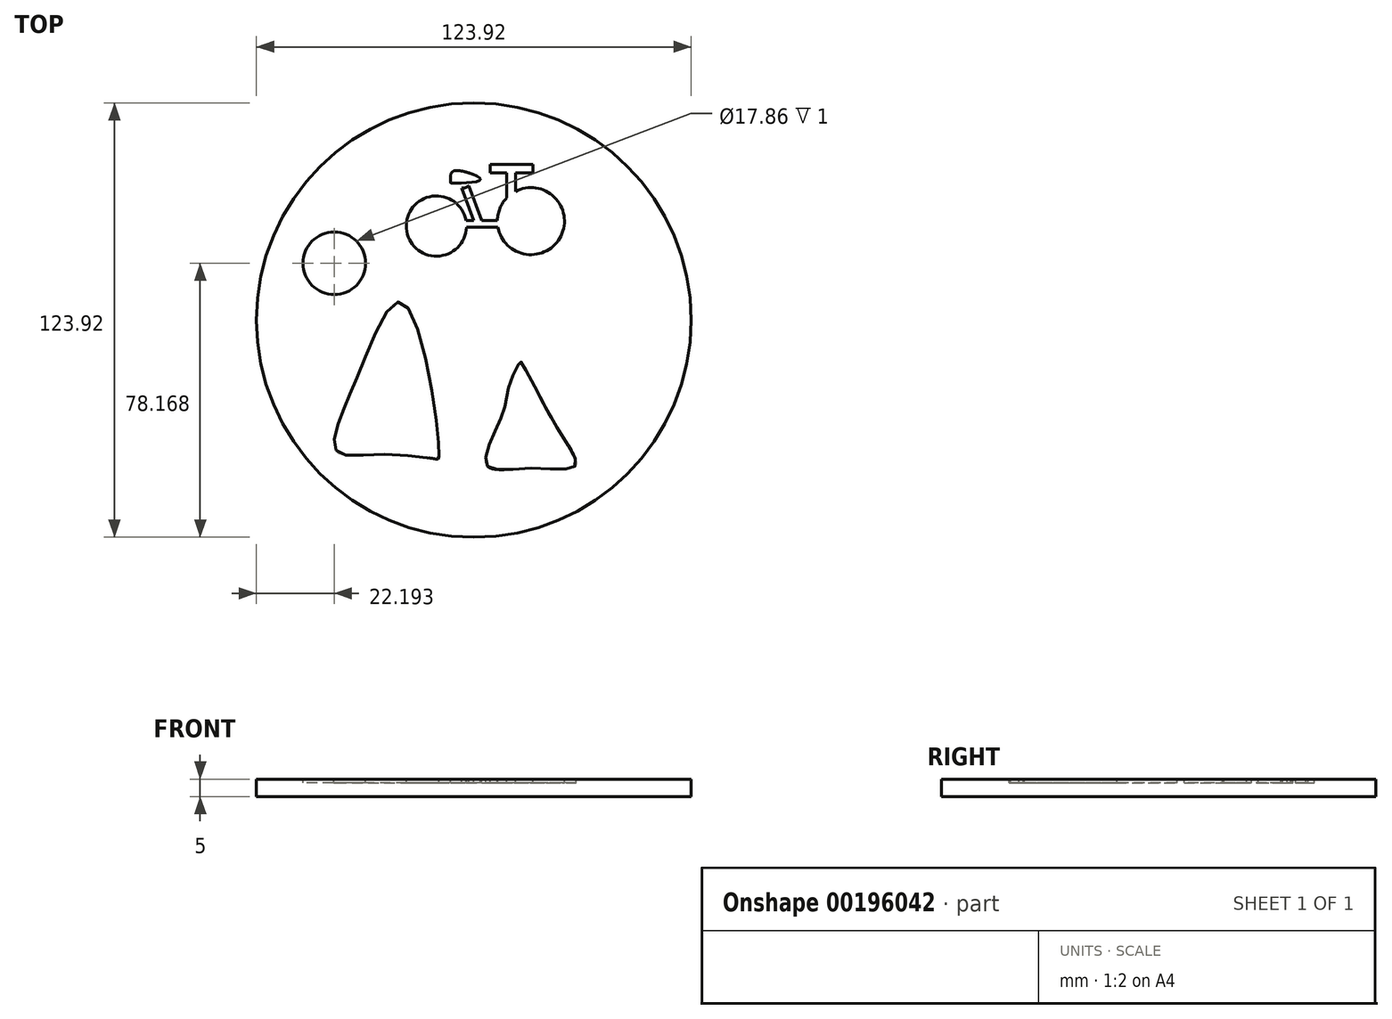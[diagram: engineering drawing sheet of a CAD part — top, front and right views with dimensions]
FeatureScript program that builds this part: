
annotation { "Feature Type Name" : "Feature", "Feature Type Description" : "" }
export const myFeature = defineFeature(function(context is Context, id is Id, definition is map)
    precondition{}
    {
        {
            var Q0;
            Q0=qCreatedBy(makeId("Top.planeOp"),FACE);
            var sketch = newSketch(context, id + "F0", { "sketchPlane" : qUnion([Q0])});
            skCircle(sketch, "E0", {"center": v(0, 0) * mm, "radius": 61.96 * mm});
            skSolve(sketch);
        }
        {
            var Q0;
            Q0 = qSketchRegion(id + "F0", true);
            extrude(context, id + "F1", {"entities" : qUnion([Q0]), "depth" : 5 * mm});
        }
        {
            var Q0;
            Q0=makeQuery(id+"F1.opExtrude","CAP_FACE",FACE,{"disambiguationData":[OSD([sQuery(id+"F0.wireOp",EDGE,"E0")])],"isStart":false});
            var sketch = newSketch(context, id + "F2", { "sketchPlane" : qUnion([Q0])});
            skFitSpline(sketch, "E1", {"points": [v(-39.3, -37.2) * mm, v(-26.67, -38.32) * mm, v(-10.39, -39.73) * mm, v(-10.1, -39.73) * mm, v(-10.95, -26.53) * mm, v(-21.06, 5.2) * mm, v(-32, -13.34) * mm, v(-37.9, -27.37) * mm, v(-39.3, -37.2) * mm]});
            skFitSpline(sketch, "E2", {"points": [v(3.93, -41.7) * mm, v(5.05, -34.11) * mm, v(8.98, -24.28) * mm, v(10.1, -18.67) * mm, v(13.2, -11.93) * mm, v(13.48, -11.93) * mm, v(23.3, -29.9) * mm, v(28.92, -41.7) * mm, v(16.84, -42.25) * mm, v(3.93, -41.7) * mm]});
            skSolve(sketch);
        }
        {
            var Q0;
            Q0=makeQuery(id+"F2.imprint","IMPRINT",FACE,{"disambiguationData":[TD([[makeQuery(id+"F2.imprint","IMPRINT",EDGE,{"derivedFrom":sQuery(id+"F2.wireOp",EDGE,"E1")}),1.0]])]});
            var Q1;
            Q1=makeQuery(id+"F2.imprint","IMPRINT",FACE,{"disambiguationData":[TD([[makeQuery(id+"F2.imprint","IMPRINT",EDGE,{"derivedFrom":sQuery(id+"F2.wireOp",EDGE,"E2")}),-1.0]])]});
            extrude(context, id + "F3", {"entities" : qUnion([Q0, Q1]), "operationType" : NewBodyOperationType.REMOVE, "oppositeDirection" : true, "depth" : 1 * mm});
        }
        {
            var Q0;
            Q0=makeQuery(id+"F1.opExtrude","CAP_FACE",FACE,{"disambiguationData":[OSD([sQuery(id+"F0.wireOp",EDGE,"E0")])],"isStart":false});
            var sketch = newSketch(context, id + "F4", { "sketchPlane" : qUnion([Q0])});
            skCircle(sketch, "E3", {"center": v(-10.67, 26.81) * mm, "radius": 8.6 * mm});
            skCircle(sketch, "E4", {"center": v(16.28, 28.21) * mm, "radius": 9.56 * mm});
            skLineSegment(sketch, "E5", {"start": v(-2.08, 26.52) * mm, "end": v(6.87, 26.52) * mm});
            skLineSegment(sketch, "E6", {"start": v(-2.23, 28.45) * mm, "end": v(6.72, 28.45) * mm});
            skLineSegment(sketch, "E7", {"start": v(0, 28.45) * mm, "end": v(-3.44, 37.62) * mm});
            skPoint(sketch, "E7.startSnap0", {"position": v(2.25, 28.45) * mm});
            skLineSegment(sketch, "E8", {"start": v(2.25, 28.45) * mm, "end": v(-1.47, 38.32) * mm});
            skLineSegment(sketch, "E9", {"start": v(-1.47, 38.32) * mm, "end": v(-3.44, 37.62) * mm});
            skFitSpline(sketch, "E10", {"points": [v(-3.44, 37.62) * mm, v(-7.8, 37.62) * mm, v(1.9, 42.95) * mm, v(-1.47, 38.32) * mm, v(-3.44, 37.62) * mm]});
            skLineSegment(sketch, "E11", {"start": v(9.4, 34.86) * mm, "end": v(9.4, 41.97) * mm});
            skLineSegment(sketch, "E12", {"start": v(9.4, 41.97) * mm, "end": v(11.86, 41.97) * mm});
            skLineSegment(sketch, "E13", {"start": v(11.86, 41.97) * mm, "end": v(11.86, 36.7) * mm});
            skLineSegment(sketch, "E14", {"start": v(11.86, 41.97) * mm, "end": v(16.92, 41.97) * mm});
            skLineSegment(sketch, "E15", {"start": v(16.92, 41.97) * mm, "end": v(16.92, 44.36) * mm});
            skLineSegment(sketch, "E16", {"start": v(16.92, 44.36) * mm, "end": v(4.7, 44.36) * mm});
            skLineSegment(sketch, "E17", {"start": v(4.7, 44.36) * mm, "end": v(4.7, 41.97) * mm});
            skLineSegment(sketch, "E18", {"start": v(4.7, 41.97) * mm, "end": v(9.4, 41.97) * mm});
            skCircle(sketch, "E19", {"center": v(-37.99, 16.8) * mm, "radius": 8.46 * mm});
            skLineSegment(sketch, "E20", {"start": v(-33.11, 26.42) * mm, "end": v(-28.01, 29.53) * mm});
            skLineSegment(sketch, "E21", {"start": v(-28.01, 29.53) * mm, "end": v(-30.73, 25.1) * mm});
            skLineSegment(sketch, "E22", {"start": v(-30.73, 25.1) * mm, "end": v(-33.11, 26.42) * mm});
            skLineSegment(sketch, "E23", {"start": v(-27.75, 19.93) * mm, "end": v(-27.75, 17.34) * mm});
            skLineSegment(sketch, "E24", {"start": v(-27.75, 17.34) * mm, "end": v(-22.05, 18.14) * mm});
            skLineSegment(sketch, "E25", {"start": v(-22.05, 18.14) * mm, "end": v(-27.75, 19.93) * mm});
            skLineSegment(sketch, "E26", {"start": v(-27.75, 12.24) * mm, "end": v(-29.07, 10) * mm});
            skLineSegment(sketch, "E27", {"start": v(-29.07, 10) * mm, "end": v(-22.78, 8.67) * mm});
            skLineSegment(sketch, "E28", {"start": v(-22.78, 8.67) * mm, "end": v(-27.75, 12.24) * mm});
            skLineSegment(sketch, "E29", {"start": v(-35.12, 5.65) * mm, "end": v(-30.16, 1.28) * mm});
            skLineSegment(sketch, "E30", {"start": v(-30.16, 1.28) * mm, "end": v(-32.28, 6.71) * mm});
            skLineSegment(sketch, "E31", {"start": v(-32.28, 6.71) * mm, "end": v(-35.12, 5.65) * mm});
            skLineSegment(sketch, "E32", {"start": v(-42.79, 7.18) * mm, "end": v(-40.55, 5.65) * mm});
            skLineSegment(sketch, "E33", {"start": v(-40.55, 5.65) * mm, "end": v(-43.67, 1.08) * mm});
            skLineSegment(sketch, "E34", {"start": v(-43.67, 1.08) * mm, "end": v(-42.79, 7.18) * mm});
            skSolve(sketch);
        }
        {
            var Q0;
            {var subQ0=sQuery(id+"F4.wireOp",EDGE,"E3");var subQ1=makeQuery(id+"F4.imprint","INTERSECT",VERTEX,{"derivedFrom":[subQ0,sQuery(id+"F4.wireOp",EDGE,"E5")]});Q0=makeQuery(id+"F4.imprint","IMPRINT",FACE,{"disambiguationData":[TD([[makeQuery(id+"F4.imprint","IMPRINT",EDGE,{"disambiguationData":[TD([[subQ1,1.0]])],"derivedFrom":subQ0}),1.0]])]});}
            var Q1;
            {var subQ0=sQuery(id+"F4.wireOp",EDGE,"E7");Q1=makeQuery(id+"F4.imprint","IMPRINT",FACE,{"disambiguationData":[TD([[makeQuery(id+"F4.imprint","IMPRINT",EDGE,{"derivedFrom":subQ0}),-1.0]])]});}
            var Q2;
            {var subQ0=sQuery(id+"F4.wireOp",EDGE,"E5");Q2=makeQuery(id+"F4.imprint","IMPRINT",FACE,{"disambiguationData":[TD([[makeQuery(id+"F4.imprint","IMPRINT",EDGE,{"derivedFrom":subQ0}),1.0]])]});}
            var Q3;
            {var subQ0=sQuery(id+"F4.wireOp",EDGE,"E4");var subQ1=makeQuery(id+"F4.imprint","INTERSECT",VERTEX,{"derivedFrom":[subQ0,sQuery(id+"F4.wireOp",EDGE,"E11")]});Q3=makeQuery(id+"F4.imprint","IMPRINT",FACE,{"disambiguationData":[TD([[makeQuery(id+"F4.imprint","IMPRINT",EDGE,{"disambiguationData":[TD([[subQ1,1.0]])],"derivedFrom":subQ0}),1.0]])]});}
            var Q4;
            {var subQ0=sQuery(id+"F4.wireOp",EDGE,"E11");Q4=makeQuery(id+"F4.imprint","IMPRINT",FACE,{"disambiguationData":[TD([[makeQuery(id+"F4.imprint","IMPRINT",EDGE,{"derivedFrom":subQ0}),-1.0]])]});}
            var Q5;
            Q5=makeQuery(id+"F4.imprint","IMPRINT",FACE,{"disambiguationData":[TD([[makeQuery(id+"F4.imprint","IMPRINT",EDGE,{"derivedFrom":sQuery(id+"F4.wireOp",EDGE,"E12")}),1.0]])]});
            extrude(context, id + "F5", {"entities" : qUnion([Q0, Q1, Q2, Q3, Q4, Q5]), "operationType" : NewBodyOperationType.REMOVE, "oppositeDirection" : true, "depth" : 1 * mm});
        }
        {
            var Q0;
            Q0=makeQuery(id+"F1.opExtrude","CAP_FACE",FACE,{"disambiguationData":[OSD([sQuery(id+"F0.wireOp",EDGE,"E0")])],"isStart":false});
            var sketch = newSketch(context, id + "F6", { "sketchPlane" : qUnion([Q0])});
            skFitSpline(sketch, "E35", {"points": [v(-4, 42.6) * mm, v(-6.5, 41.72) * mm, v(-6.63, 39.22) * mm, v(-6.5, 39.1) * mm, v(1.88, 39.97) * mm, v(-4, 42.6) * mm]});
            skSolve(sketch);
        }
        {
            var Q0;
            Q0=makeQuery(id+"F6.imprint","IMPRINT",FACE,{"disambiguationData":[TD([[makeQuery(id+"F6.imprint","IMPRINT",EDGE,{"derivedFrom":sQuery(id+"F6.wireOp",EDGE,"E35")}),1.0]])]});
            extrude(context, id + "F7", {"entities" : qUnion([Q0]), "operationType" : NewBodyOperationType.REMOVE, "oppositeDirection" : true, "depth" : 1 * mm});
        }
        {
            var Q0;
            Q0=makeQuery(id+"F1.opExtrude","CAP_FACE",FACE,{"disambiguationData":[OSD([sQuery(id+"F0.wireOp",EDGE,"E0")])],"isStart":false});
            var sketch = newSketch(context, id + "F8", { "sketchPlane" : qUnion([Q0])});
            skCircle(sketch, "E36", {"center": v(-39.77, 16.2) * mm, "radius": 8.93 * mm});
            skSolve(sketch);
        }
        {
            var Q0;
            Q0=makeQuery(id+"F8.imprint","IMPRINT",FACE,{"disambiguationData":[TD([[makeQuery(id+"F8.imprint","IMPRINT",EDGE,{"derivedFrom":sQuery(id+"F8.wireOp",EDGE,"E36")}),1.0]])]});
            extrude(context, id + "F9", {"entities" : qUnion([Q0]), "operationType" : NewBodyOperationType.REMOVE, "oppositeDirection" : true, "depth" : 1 * mm});
        }
    });
